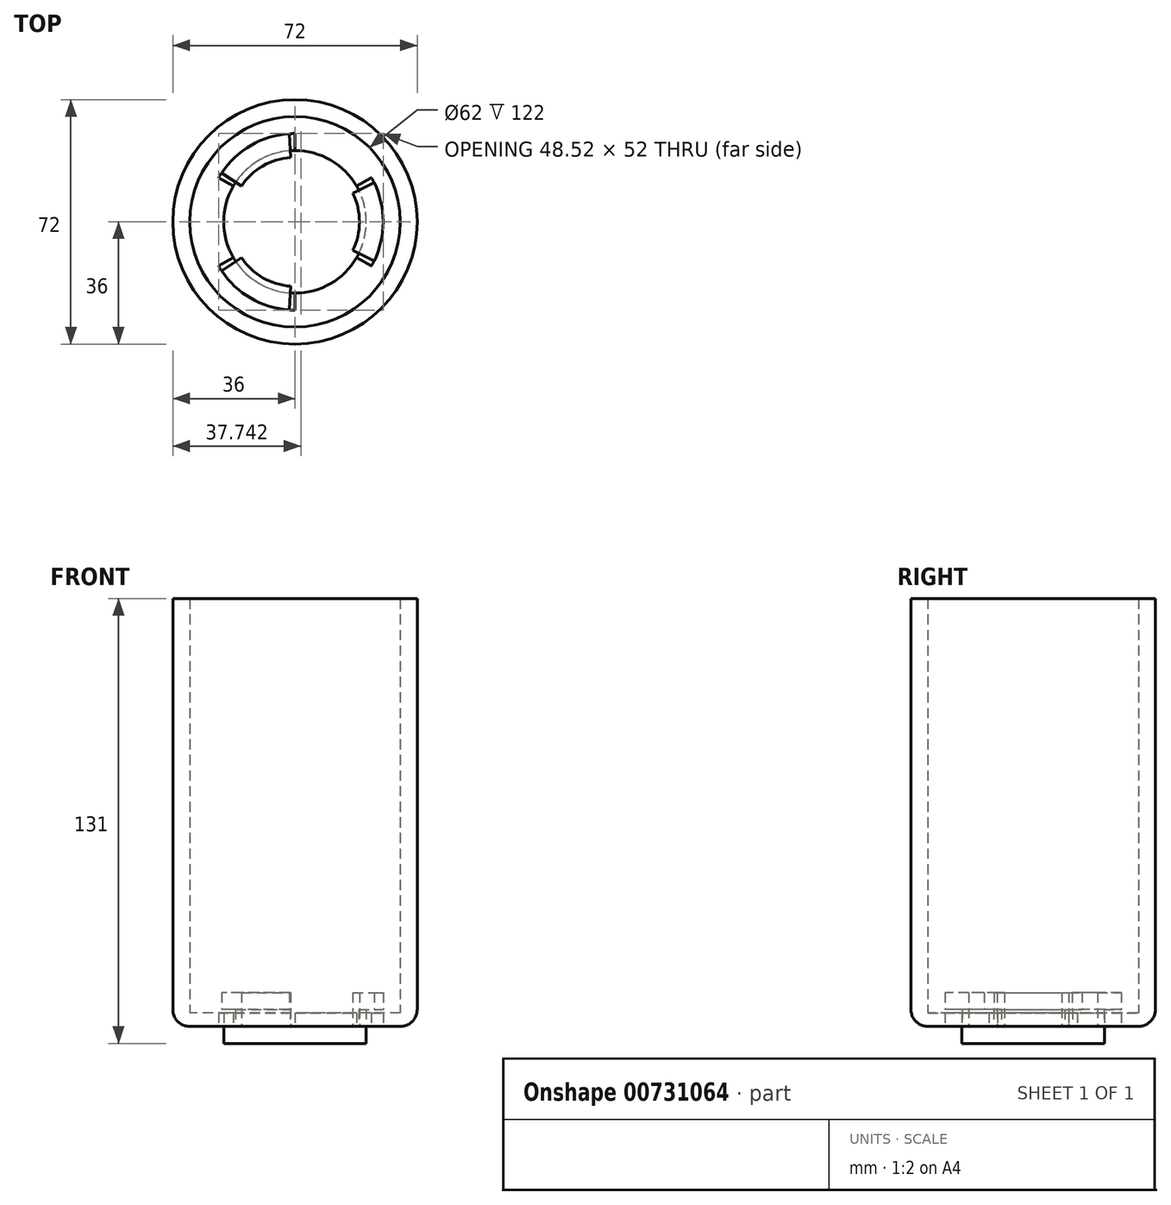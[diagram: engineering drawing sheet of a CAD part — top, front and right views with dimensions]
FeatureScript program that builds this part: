
annotation { "Feature Type Name" : "Feature", "Feature Type Description" : "" }
export const myFeature = defineFeature(function(context is Context, id is Id, definition is map)
    precondition{}
    {
        {
            var Q0;
            Q0=qCreatedBy(makeId("Top.planeOp"),FACE);
            var sketch = newSketch(context, id + "F0", { "sketchPlane" : qUnion([Q0])});
            skCircle(sketch, "E0", {"center": v(0, 0) * mm, "radius": 36 * mm});
            skCircle(sketch, "E1", {"center": v(0, 0) * mm, "radius": 31 * mm});
            skLineSegment(sketch, "E2", {"start": v(0, 31) * mm, "end": v(0, 0) * mm, "construction": true});
            skLineSegment(sketch, "E3", {"start": v(26.85, 15.5) * mm, "end": v(18.19, 10.5) * mm});
            skLineSegment(sketch, "E4", {"start": v(0, 31) * mm, "end": v(0, 21) * mm});
            skLineSegment(sketch, "E5.1.0", {"start": v(-26.85, 15.5) * mm, "end": v(-18.19, 10.5) * mm});
            skLineSegment(sketch, "E5.1.1", {"start": v(-26.85, -15.5) * mm, "end": v(-18.19, -10.5) * mm});
            skLineSegment(sketch, "E5.2.0", {"start": v(0, -31) * mm, "end": v(0, -21) * mm});
            skLineSegment(sketch, "E5.2.1", {"start": v(26.85, -15.5) * mm, "end": v(18.19, -10.5) * mm});
            skCircle(sketch, "E6", {"center": v(0, 0) * mm, "radius": 26 * mm});
            skCircle(sketch, "E7", {"center": v(0, 0) * mm, "radius": 19 * mm});
            skLineSegment(sketch, "E8", {"start": v(0, 0) * mm, "end": v(-2, 30.94) * mm});
            skLineSegment(sketch, "E9", {"start": v(0, 0) * mm, "end": v(27.8, 13.74) * mm});
            skLineSegment(sketch, "E10.1.0", {"start": v(0, 0) * mm, "end": v(-25.8, -17.2) * mm});
            skLineSegment(sketch, "E10.1.1", {"start": v(0, 0) * mm, "end": v(-25.8, 17.2) * mm});
            skLineSegment(sketch, "E10.2.0", {"start": v(0, 0) * mm, "end": v(27.8, -13.74) * mm});
            skLineSegment(sketch, "E10.2.1", {"start": v(0, 0) * mm, "end": v(-2, -30.94) * mm});
            skCircle(sketch, "E11", {"center": v(0, 0) * mm, "radius": 21 * mm});
            skSolve(sketch);
        }
        {
            var Q0;
            Q0 = qSketchRegion(id + "F0", true);
            extrude(context, id + "F1", {"entities" : qUnion([Q0]), "depth" : 126 * mm, "offsetDistance" : 25 * mm});
        }
        {
            var Q0;
            {var subQ0=sQuery(id+"F0.wireOp",EDGE,"E5.2.0");Q0=makeQuery(id+"F0.imprint","IMPRINT",FACE,{"disambiguationData":[TD([[makeQuery(id+"F0.imprint","IMPRINT",EDGE,{"derivedFrom":subQ0}),-1.0]])]});}
            var Q1;
            Q1=makeQuery(id+"F0.imprint","IMPRINT",FACE,{"disambiguationData":[TD([[makeQuery(id+"F0.imprint","IMPRINT",EDGE,{"derivedFrom":sQuery(id+"F0.wireOp",EDGE,"9ivIQBOw-K5pD-WZSV-468c-jCQv9gzagSr3")}),-1.0]])]});
            var Q2;
            {var subQ0=sQuery(id+"F0.wireOp",EDGE,"E5.1.0");Q2=makeQuery(id+"F0.imprint","IMPRINT",FACE,{"disambiguationData":[TD([[makeQuery(id+"F0.imprint","IMPRINT",EDGE,{"derivedFrom":subQ0}),-1.0]])]});}
            var Q3;
            {var subQ0=sQuery(id+"F0.wireOp",EDGE,"E5.1.1");var subQ1=sQuery(id+"F0.wireOp",EDGE,"E1");var subQ2=makeQuery(id+"F0.imprint","INTERSECT",VERTEX,{"derivedFrom":[subQ1,subQ0]});Q3=makeQuery(id+"F0.imprint","IMPRINT",FACE,{"disambiguationData":[TD([[makeQuery(id+"F0.imprint","IMPRINT",EDGE,{"disambiguationData":[TD([[subQ2,-1.0]])],"derivedFrom":subQ1}),1.0]])]});}
            var Q4;
            {var subQ0=sQuery(id+"F0.wireOp",EDGE,"E4");var subQ1=sQuery(id+"F0.wireOp",EDGE,"E1");var subQ2=makeQuery(id+"F0.imprint","INTERSECT",VERTEX,{"derivedFrom":[subQ1,subQ0]});Q4=makeQuery(id+"F0.imprint","IMPRINT",FACE,{"disambiguationData":[TD([[makeQuery(id+"F0.imprint","IMPRINT",EDGE,{"disambiguationData":[TD([[subQ2,-1.0]])],"derivedFrom":subQ1}),1.0]])]});}
            var Q5;
            {var subQ0=sQuery(id+"F0.wireOp",EDGE,"E3");var subQ1=sQuery(id+"F0.wireOp",EDGE,"E1");var subQ2=makeQuery(id+"F0.imprint","INTERSECT",VERTEX,{"derivedFrom":[subQ1,subQ0]});Q5=makeQuery(id+"F0.imprint","IMPRINT",FACE,{"disambiguationData":[TD([[makeQuery(id+"F0.imprint","IMPRINT",EDGE,{"disambiguationData":[TD([[subQ2,-1.0]])],"derivedFrom":subQ1}),1.0]])]});}
            var Q6;
            {var subQ0=sQuery(id+"F0.wireOp",EDGE,"E8");var subQ1=sQuery(id+"F0.wireOp",EDGE,"E1");var subQ2=makeQuery(id+"F0.imprint","INTERSECT",VERTEX,{"derivedFrom":[subQ1,subQ0]});Q6=makeQuery(id+"F0.imprint","IMPRINT",FACE,{"disambiguationData":[TD([[makeQuery(id+"F0.imprint","IMPRINT",EDGE,{"disambiguationData":[TD([[subQ2,-1.0]])],"derivedFrom":subQ1}),1.0]])]});}
            var Q7;
            {var subQ0=sQuery(id+"F0.wireOp",EDGE,"E11");var subQ1=sQuery(id+"F0.wireOp",EDGE,"E3");var subQ2=makeQuery(id+"F0.imprint","INTERSECT",VERTEX,{"derivedFrom":[subQ1,subQ0]});Q7=makeQuery(id+"F0.imprint","IMPRINT",FACE,{"disambiguationData":[TD([[makeQuery(id+"F0.imprint","IMPRINT",EDGE,{"disambiguationData":[TD([[subQ2,1.0]])],"derivedFrom":subQ1}),-1.0]])]});}
            var Q8;
            {var subQ0=sQuery(id+"F0.wireOp",EDGE,"E5.1.0");var subQ1=sQuery(id+"F0.wireOp",EDGE,"E1");var subQ2=makeQuery(id+"F0.imprint","INTERSECT",VERTEX,{"derivedFrom":[subQ1,subQ0]});Q8=makeQuery(id+"F0.imprint","IMPRINT",FACE,{"disambiguationData":[TD([[makeQuery(id+"F0.imprint","IMPRINT",EDGE,{"disambiguationData":[TD([[subQ2,1.0]])],"derivedFrom":subQ1}),1.0]])]});}
            var Q9;
            {var subQ0=sQuery(id+"F0.wireOp",EDGE,"E3");var subQ1=sQuery(id+"F0.wireOp",EDGE,"E1");var subQ2=makeQuery(id+"F0.imprint","INTERSECT",VERTEX,{"derivedFrom":[subQ1,subQ0]});Q9=makeQuery(id+"F0.imprint","IMPRINT",FACE,{"disambiguationData":[TD([[makeQuery(id+"F0.imprint","IMPRINT",EDGE,{"disambiguationData":[TD([[subQ2,1.0]])],"derivedFrom":subQ1}),1.0]])]});}
            var Q10;
            {var subQ0=sQuery(id+"F0.wireOp",EDGE,"E9");var subQ1=sQuery(id+"F0.wireOp",EDGE,"E1");var subQ2=makeQuery(id+"F0.imprint","INTERSECT",VERTEX,{"derivedFrom":[subQ1,subQ0]});Q10=makeQuery(id+"F0.imprint","IMPRINT",FACE,{"disambiguationData":[TD([[makeQuery(id+"F0.imprint","IMPRINT",EDGE,{"disambiguationData":[TD([[subQ2,1.0]])],"derivedFrom":subQ1}),1.0]])]});}
            var Q11;
            {var subQ0=sQuery(id+"F0.wireOp",EDGE,"E5.2.1");var subQ1=sQuery(id+"F0.wireOp",EDGE,"E1");var subQ2=makeQuery(id+"F0.imprint","INTERSECT",VERTEX,{"derivedFrom":[subQ1,subQ0]});Q11=makeQuery(id+"F0.imprint","IMPRINT",FACE,{"disambiguationData":[TD([[makeQuery(id+"F0.imprint","IMPRINT",EDGE,{"disambiguationData":[TD([[subQ2,-1.0]])],"derivedFrom":subQ1}),1.0]])]});}
            var Q12;
            {var subQ0=sQuery(id+"F0.wireOp",EDGE,"E5.2.0");var subQ1=sQuery(id+"F0.wireOp",EDGE,"E1");var subQ2=makeQuery(id+"F0.imprint","INTERSECT",VERTEX,{"derivedFrom":[subQ1,subQ0]});Q12=makeQuery(id+"F0.imprint","IMPRINT",FACE,{"disambiguationData":[TD([[makeQuery(id+"F0.imprint","IMPRINT",EDGE,{"disambiguationData":[TD([[subQ2,1.0]])],"derivedFrom":subQ1}),1.0]])]});}
            var Q13;
            {var subQ0=sQuery(id+"F0.wireOp",EDGE,"E10.1.0");var subQ1=sQuery(id+"F0.wireOp",EDGE,"E1");var subQ2=makeQuery(id+"F0.imprint","INTERSECT",VERTEX,{"derivedFrom":[subQ1,subQ0]});Q13=makeQuery(id+"F0.imprint","IMPRINT",FACE,{"disambiguationData":[TD([[makeQuery(id+"F0.imprint","IMPRINT",EDGE,{"disambiguationData":[TD([[subQ2,-1.0]])],"derivedFrom":subQ1}),1.0]])]});}
            extrude(context, id + "F2", {"entities" : qUnion([Q0, Q1, Q2, Q3, Q4, Q5, Q6, Q7, Q8, Q9, Q10, Q11, Q12, Q13]), "operationType" : NewBodyOperationType.ADD, "depth" : 4 * mm, "offsetDistance" : 25 * mm});
        }
        {
            var Q0;
            Q0=makeQuery(id+"F1.opExtrude","CAP_EDGE",EDGE,{"disambiguationData":[OSD([sQuery(id+"F0.wireOp",EDGE,"E0")])],"isStart":true});
            fillet(context, id + "F3", {"entities" : qUnion([Q0]), "radius" : 5 * mm, "tangentPropagation" : true, "allowEdgeOverflow" : false});
        }
        {
            var Q0;
            {var subQ0=sQuery(id+"F0.wireOp",EDGE,"E9");var subQ1=sQuery(id+"F0.wireOp",EDGE,"E6");var subQ2=makeQuery(id+"F0.imprint","INTERSECT",VERTEX,{"derivedFrom":[subQ1,subQ0]});Q0=makeQuery(id+"F0.imprint","IMPRINT",FACE,{"disambiguationData":[TD([[makeQuery(id+"F0.imprint","IMPRINT",EDGE,{"disambiguationData":[TD([[subQ2,1.0]])],"derivedFrom":subQ1}),1.0]])]});}
            var Q1;
            {var subQ0=sQuery(id+"F0.wireOp",EDGE,"E10.1.0");var subQ1=sQuery(id+"F0.wireOp",EDGE,"E6");var subQ2=makeQuery(id+"F0.imprint","INTERSECT",VERTEX,{"derivedFrom":[subQ1,subQ0]});Q1=makeQuery(id+"F0.imprint","IMPRINT",FACE,{"disambiguationData":[TD([[makeQuery(id+"F0.imprint","IMPRINT",EDGE,{"disambiguationData":[TD([[subQ2,-1.0]])],"derivedFrom":subQ1}),1.0]])]});}
            var Q2;
            {var subQ0=sQuery(id+"F0.wireOp",EDGE,"E8");var subQ1=sQuery(id+"F0.wireOp",EDGE,"E6");var subQ2=makeQuery(id+"F0.imprint","INTERSECT",VERTEX,{"derivedFrom":[subQ1,subQ0]});Q2=makeQuery(id+"F0.imprint","IMPRINT",FACE,{"disambiguationData":[TD([[makeQuery(id+"F0.imprint","IMPRINT",EDGE,{"disambiguationData":[TD([[subQ2,-1.0]])],"derivedFrom":subQ1}),1.0]])]});}
            var Q3;
            {var subQ0=sQuery(id+"F0.wireOp",EDGE,"E8");var subQ1=sQuery(id+"F0.wireOp",EDGE,"E7");var subQ2=makeQuery(id+"F0.imprint","INTERSECT",VERTEX,{"derivedFrom":[subQ1,subQ0]});Q3=makeQuery(id+"F0.imprint","IMPRINT",FACE,{"disambiguationData":[TD([[makeQuery(id+"F0.imprint","IMPRINT",EDGE,{"disambiguationData":[TD([[subQ2,-1.0]])],"derivedFrom":subQ1}),-1.0]])]});}
            var Q4;
            {var subQ0=sQuery(id+"F0.wireOp",EDGE,"E10.1.0");var subQ1=sQuery(id+"F0.wireOp",EDGE,"E7");var subQ2=makeQuery(id+"F0.imprint","INTERSECT",VERTEX,{"derivedFrom":[subQ1,subQ0]});Q4=makeQuery(id+"F0.imprint","IMPRINT",FACE,{"disambiguationData":[TD([[makeQuery(id+"F0.imprint","IMPRINT",EDGE,{"disambiguationData":[TD([[subQ2,-1.0]])],"derivedFrom":subQ1}),-1.0]])]});}
            var Q5;
            {var subQ0=sQuery(id+"F0.wireOp",EDGE,"E9");var subQ1=sQuery(id+"F0.wireOp",EDGE,"E7");var subQ2=makeQuery(id+"F0.imprint","INTERSECT",VERTEX,{"derivedFrom":[subQ1,subQ0]});Q5=makeQuery(id+"F0.imprint","IMPRINT",FACE,{"disambiguationData":[TD([[makeQuery(id+"F0.imprint","IMPRINT",EDGE,{"disambiguationData":[TD([[subQ2,1.0]])],"derivedFrom":subQ1}),-1.0]])]});}
            extrude(context, id + "F4", {"entities" : qUnion([Q0, Q1, Q2, Q3, Q4, Q5]), "depth" : 10 * mm, "offsetDistance" : 25 * mm});
        }
        {
            var Q0;
            {var subQ0=sQuery(id+"F0.wireOp",EDGE,"E10.1.0");var subQ1=sQuery(id+"F0.wireOp",EDGE,"E6");var subQ2=makeQuery(id+"F0.imprint","INTERSECT",VERTEX,{"derivedFrom":[subQ1,subQ0]});Q0=makeQuery(id+"F0.imprint","IMPRINT",FACE,{"disambiguationData":[TD([[makeQuery(id+"F0.imprint","IMPRINT",EDGE,{"disambiguationData":[TD([[subQ2,-1.0]])],"derivedFrom":subQ1}),1.0]])]});}
            var Q1;
            {var subQ0=sQuery(id+"F0.wireOp",EDGE,"E9");var subQ1=sQuery(id+"F0.wireOp",EDGE,"E6");var subQ2=makeQuery(id+"F0.imprint","INTERSECT",VERTEX,{"derivedFrom":[subQ1,subQ0]});Q1=makeQuery(id+"F0.imprint","IMPRINT",FACE,{"disambiguationData":[TD([[makeQuery(id+"F0.imprint","IMPRINT",EDGE,{"disambiguationData":[TD([[subQ2,1.0]])],"derivedFrom":subQ1}),1.0]])]});}
            var Q2;
            {var subQ0=sQuery(id+"F0.wireOp",EDGE,"E8");var subQ1=sQuery(id+"F0.wireOp",EDGE,"E6");var subQ2=makeQuery(id+"F0.imprint","INTERSECT",VERTEX,{"derivedFrom":[subQ1,subQ0]});Q2=makeQuery(id+"F0.imprint","IMPRINT",FACE,{"disambiguationData":[TD([[makeQuery(id+"F0.imprint","IMPRINT",EDGE,{"disambiguationData":[TD([[subQ2,-1.0]])],"derivedFrom":subQ1}),1.0]])]});}
            extrude(context, id + "F5", {"entities" : qUnion([Q0, Q1, Q2]), "operationType" : NewBodyOperationType.REMOVE, "depth" : 5 * mm, "offsetDistance" : 25 * mm});
        }
        {
            var Q0;
            {var subQ0=sQuery(id+"F0.wireOp",EDGE,"E10.1.0");var subQ1=sQuery(id+"F0.wireOp",EDGE,"E7");var subQ2=makeQuery(id+"F0.imprint","INTERSECT",VERTEX,{"derivedFrom":[subQ1,subQ0]});Q0=makeQuery(id+"F0.imprint","IMPRINT",FACE,{"disambiguationData":[TD([[makeQuery(id+"F0.imprint","IMPRINT",EDGE,{"disambiguationData":[TD([[subQ2,-1.0]])],"derivedFrom":subQ1}),1.0]])]});}
            var Q1;
            {var subQ0=sQuery(id+"F0.wireOp",EDGE,"E10.2.1");var subQ1=sQuery(id+"F0.wireOp",EDGE,"E7");var subQ2=makeQuery(id+"F0.imprint","INTERSECT",VERTEX,{"derivedFrom":[subQ1,subQ0]});Q1=makeQuery(id+"F0.imprint","IMPRINT",FACE,{"disambiguationData":[TD([[makeQuery(id+"F0.imprint","IMPRINT",EDGE,{"disambiguationData":[TD([[subQ2,-1.0]])],"derivedFrom":subQ1}),1.0]])]});}
            var Q2;
            {var subQ0=sQuery(id+"F0.wireOp",EDGE,"E9");var subQ1=sQuery(id+"F0.wireOp",EDGE,"E7");var subQ2=makeQuery(id+"F0.imprint","INTERSECT",VERTEX,{"derivedFrom":[subQ1,subQ0]});Q2=makeQuery(id+"F0.imprint","IMPRINT",FACE,{"disambiguationData":[TD([[makeQuery(id+"F0.imprint","IMPRINT",EDGE,{"disambiguationData":[TD([[subQ2,1.0]])],"derivedFrom":subQ1}),1.0]])]});}
            var Q3;
            {var subQ0=sQuery(id+"F0.wireOp",EDGE,"E8");var subQ1=sQuery(id+"F0.wireOp",EDGE,"E7");var subQ2=makeQuery(id+"F0.imprint","INTERSECT",VERTEX,{"derivedFrom":[subQ1,subQ0]});Q3=makeQuery(id+"F0.imprint","IMPRINT",FACE,{"disambiguationData":[TD([[makeQuery(id+"F0.imprint","IMPRINT",EDGE,{"disambiguationData":[TD([[subQ2,1.0]])],"derivedFrom":subQ1}),1.0]])]});}
            var Q4;
            {var subQ0=sQuery(id+"F0.wireOp",EDGE,"E8");var subQ1=sQuery(id+"F0.wireOp",EDGE,"E7");var subQ2=makeQuery(id+"F0.imprint","INTERSECT",VERTEX,{"derivedFrom":[subQ1,subQ0]});Q4=makeQuery(id+"F0.imprint","IMPRINT",FACE,{"disambiguationData":[TD([[makeQuery(id+"F0.imprint","IMPRINT",EDGE,{"disambiguationData":[TD([[subQ2,-1.0]])],"derivedFrom":subQ1}),1.0]])]});}
            var Q5;
            {var subQ0=sQuery(id+"F0.wireOp",EDGE,"E10.1.1");var subQ1=sQuery(id+"F0.wireOp",EDGE,"E7");var subQ2=makeQuery(id+"F0.imprint","INTERSECT",VERTEX,{"derivedFrom":[subQ1,subQ0]});Q5=makeQuery(id+"F0.imprint","IMPRINT",FACE,{"disambiguationData":[TD([[makeQuery(id+"F0.imprint","IMPRINT",EDGE,{"disambiguationData":[TD([[subQ2,-1.0]])],"derivedFrom":subQ1}),1.0]])]});}
            var Q6;
            {var subQ0=sQuery(id+"F0.wireOp",EDGE,"E10.1.0");var subQ1=sQuery(id+"F0.wireOp",EDGE,"E7");var subQ2=makeQuery(id+"F0.imprint","INTERSECT",VERTEX,{"derivedFrom":[subQ1,subQ0]});Q6=makeQuery(id+"F0.imprint","IMPRINT",FACE,{"disambiguationData":[TD([[makeQuery(id+"F0.imprint","IMPRINT",EDGE,{"disambiguationData":[TD([[subQ2,-1.0]])],"derivedFrom":subQ1}),-1.0]])]});}
            var Q7;
            {var subQ0=sQuery(id+"F0.wireOp",EDGE,"E10.2.1");var subQ1=sQuery(id+"F0.wireOp",EDGE,"E7");var subQ2=makeQuery(id+"F0.imprint","INTERSECT",VERTEX,{"derivedFrom":[subQ1,subQ0]});Q7=makeQuery(id+"F0.imprint","IMPRINT",FACE,{"disambiguationData":[TD([[makeQuery(id+"F0.imprint","IMPRINT",EDGE,{"disambiguationData":[TD([[subQ2,-1.0]])],"derivedFrom":subQ1}),-1.0]])]});}
            var Q8;
            {var subQ0=sQuery(id+"F0.wireOp",EDGE,"E9");var subQ1=sQuery(id+"F0.wireOp",EDGE,"E7");var subQ2=makeQuery(id+"F0.imprint","INTERSECT",VERTEX,{"derivedFrom":[subQ1,subQ0]});Q8=makeQuery(id+"F0.imprint","IMPRINT",FACE,{"disambiguationData":[TD([[makeQuery(id+"F0.imprint","IMPRINT",EDGE,{"disambiguationData":[TD([[subQ2,1.0]])],"derivedFrom":subQ1}),-1.0]])]});}
            var Q9;
            {var subQ1=sQuery(id+"F0.wireOp",EDGE,"E7");var subQ5=sQuery(id+"F0.wireOp",EDGE,"E8");var subQ6=makeQuery(id+"F0.imprint","INTERSECT",VERTEX,{"derivedFrom":[subQ1,subQ5]});Q9=makeQuery(id+"F0.imprint","IMPRINT",FACE,{"disambiguationData":[TD([[makeQuery(id+"F0.imprint","IMPRINT",EDGE,{"disambiguationData":[TD([[subQ6,1.0]])],"derivedFrom":subQ1}),-1.0]])]});}
            var Q10;
            {var subQ0=sQuery(id+"F0.wireOp",EDGE,"E8");var subQ1=sQuery(id+"F0.wireOp",EDGE,"E7");var subQ2=makeQuery(id+"F0.imprint","INTERSECT",VERTEX,{"derivedFrom":[subQ1,subQ0]});Q10=makeQuery(id+"F0.imprint","IMPRINT",FACE,{"disambiguationData":[TD([[makeQuery(id+"F0.imprint","IMPRINT",EDGE,{"disambiguationData":[TD([[subQ2,-1.0]])],"derivedFrom":subQ1}),-1.0]])]});}
            var Q11;
            {var subQ2=sQuery(id+"F0.wireOp",EDGE,"E10.1.1");var subQ4=sQuery(id+"F0.wireOp",EDGE,"E7");var subQ5=makeQuery(id+"F0.imprint","INTERSECT",VERTEX,{"derivedFrom":[subQ4,subQ2]});Q11=makeQuery(id+"F0.imprint","IMPRINT",FACE,{"disambiguationData":[TD([[makeQuery(id+"F0.imprint","IMPRINT",EDGE,{"disambiguationData":[TD([[subQ5,-1.0]])],"derivedFrom":subQ4}),-1.0]])]});}
            extrude(context, id + "F6", {"entities" : qUnion([Q0, Q1, Q2, Q3, Q4, Q5, Q6, Q7, Q8, Q9, Q10, Q11]), "operationType" : NewBodyOperationType.ADD, "oppositeDirection" : true, "depth" : 5 * mm, "offsetDistance" : 25 * mm});
        }
    });
